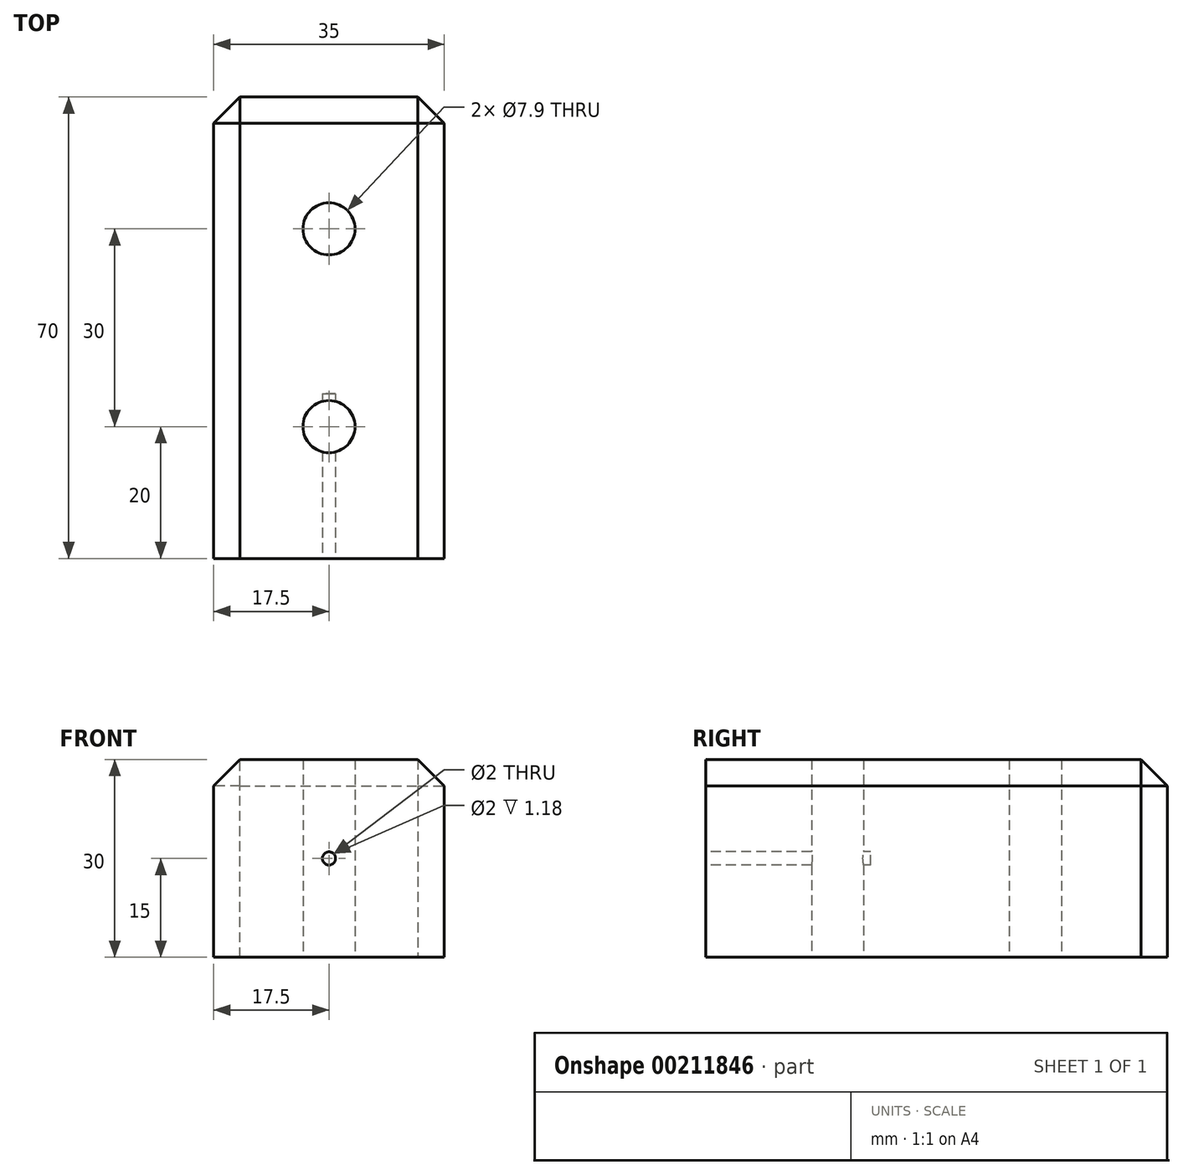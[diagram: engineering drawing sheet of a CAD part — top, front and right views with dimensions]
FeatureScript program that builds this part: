
annotation { "Feature Type Name" : "Feature", "Feature Type Description" : "" }
export const myFeature = defineFeature(function(context is Context, id is Id, definition is map)
    precondition{}
    {
        {
            var Q0;
            Q0=qCreatedBy(makeId("Top.planeOp"),FACE);
            var sketch = newSketch(context, id + "F0", { "sketchPlane" : qUnion([Q0])});
            skLineSegment(sketch, "E0.bottom", {"start": v(-17.5, 35) * mm, "end": v(17.5, 35) * mm});
            skLineSegment(sketch, "E0.top", {"start": v(-17.5, -35) * mm, "end": v(17.5, -35) * mm});
            skLineSegment(sketch, "E0.left", {"start": v(-17.5, 35) * mm, "end": v(-17.5, -35) * mm});
            skLineSegment(sketch, "E0.right", {"start": v(17.5, 35) * mm, "end": v(17.5, -35) * mm});
            skLineSegment(sketch, "E1", {"start": v(0, 0) * mm, "end": v(17.5, 0) * mm, "construction": true});
            skLineSegment(sketch, "E2", {"start": v(0, 0) * mm, "end": v(-17.5, 0) * mm, "construction": true});
            skLineSegment(sketch, "E3", {"start": v(0, 0) * mm, "end": v(0, 35) * mm, "construction": true});
            skLineSegment(sketch, "E4", {"start": v(0, 0) * mm, "end": v(0, -35) * mm, "construction": true});
            skCircle(sketch, "E5", {"center": v(0, 15) * mm, "radius": 3.95 * mm});
            skCircle(sketch, "E6", {"center": v(0, -15) * mm, "radius": 3.95 * mm});
            skSolve(sketch);
        }
        {
            var Q0;
            Q0=makeQuery(id+"F0.imprint","IMPRINT",FACE,{"disambiguationData":[TD([[makeQuery(id+"F0.imprint","IMPRINT",EDGE,{"derivedFrom":sQuery(id+"F0.wireOp",EDGE,"E0.bottom")}),-1.0]])]});
            extrude(context, id + "F1", {"entities" : qUnion([Q0]), "depth" : 30 * mm, "offsetDistance" : 25 * mm});
        }
        {
            var Q0;
            Q0=makeQuery(id+"F1.opExtrude","CAP_EDGE",EDGE,{"disambiguationData":[OSD([sQuery(id+"F0.wireOp",EDGE,"E0.bottom")])],"isStart":false});
            var Q1;
            Q1=makeQuery(id+"F1.opExtrude","CAP_EDGE",EDGE,{"disambiguationData":[OSD([sQuery(id+"F0.wireOp",EDGE,"E0.right")])],"isStart":false});
            var Q2;
            Q2=makeQuery(id+"F1.opExtrude","CAP_EDGE",EDGE,{"disambiguationData":[OSD([sQuery(id+"F0.wireOp",EDGE,"E0.left")])],"isStart":false});
            var Q3;
            Q3=makeQuery(id+"F1.opExtrude","SWEPT_EDGE",EDGE,{"disambiguationData":[OSD([sQuery(id+"F0.wireOp",EDGE,"E0.bottom"),sQuery(id+"F0.wireOp",EDGE,"E0.right")])]});
            var Q4;
            Q4=makeQuery(id+"F1.opExtrude","SWEPT_EDGE",EDGE,{"disambiguationData":[OSD([sQuery(id+"F0.wireOp",EDGE,"E0.bottom"),sQuery(id+"F0.wireOp",EDGE,"E0.left")])]});
            chamfer(context, id + "F2", {"entities" : qUnion([Q0, Q1, Q2, Q3, Q4]), "width" : 4 * mm, "tangentPropagation" : true});
        }
        {
            var Q0;
            Q0=makeQuery(id+"F1.opExtrude","SWEPT_FACE",FACE,{"disambiguationData":[OSD([sQuery(id+"F0.wireOp",EDGE,"E0.top")])]});
            var sketch = newSketch(context, id + "F3", { "sketchPlane" : qUnion([Q0])});
            skCircle(sketch, "E7", {"center": v(0, 15) * mm, "radius": 1 * mm});
            skLineSegment(sketch, "E8", {"start": v(0, 15) * mm, "end": v(17.5, 15) * mm, "construction": true});
            skLineSegment(sketch, "E9", {"start": v(0, 15) * mm, "end": v(-17.5, 15) * mm, "construction": true});
            skSolve(sketch);
        }
        {
            var Q0;
            Q0=makeQuery(id+"F3.imprint","IMPRINT",FACE,{"disambiguationData":[TD([[makeQuery(id+"F3.imprint","IMPRINT",EDGE,{"derivedFrom":sQuery(id+"F3.wireOp",EDGE,"E7")}),1.0]])]});
            extrude(context, id + "F4", {"entities" : qUnion([Q0]), "operationType" : NewBodyOperationType.REMOVE, "oppositeDirection" : true, "depth" : 25 * mm, "offsetDistance" : 25 * mm});
        }
    });
